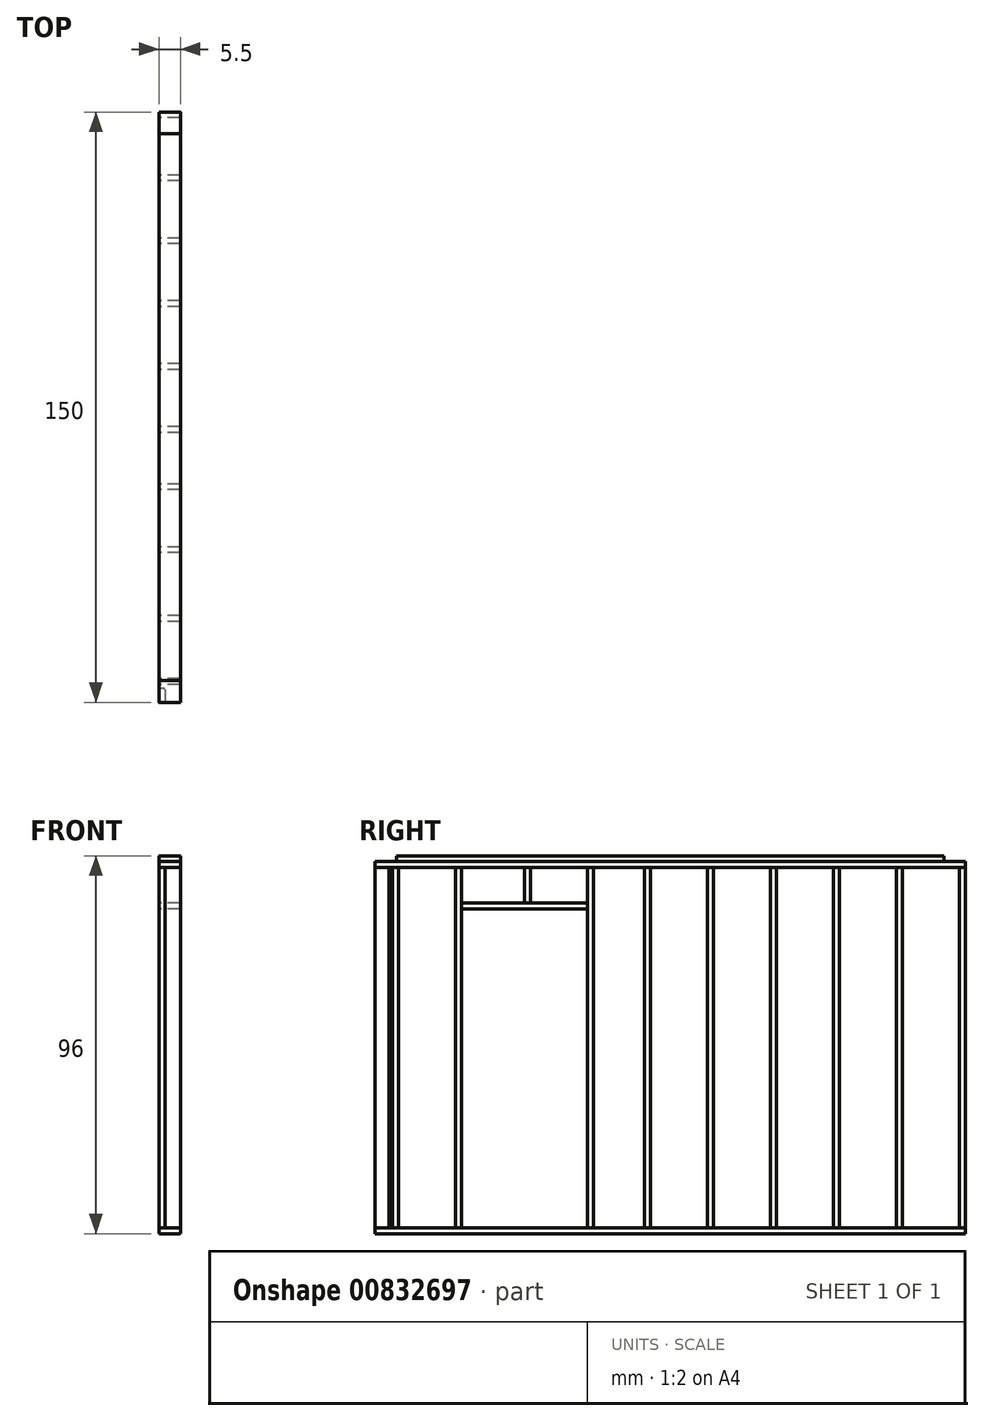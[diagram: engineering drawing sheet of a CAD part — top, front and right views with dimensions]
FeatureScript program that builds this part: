
annotation { "Feature Type Name" : "Feature", "Feature Type Description" : "" }
export const myFeature = defineFeature(function(context is Context, id is Id, definition is map)
    precondition{}
    {
        {
            var Q0;
            Q0=qCreatedBy(makeId("Right.planeOp"),FACE);
            var sketch = newSketch(context, id + "F0", { "sketchPlane" : qUnion([Q0])});
            skLineSegment(sketch, "E0.bottom", {"start": v(-65.32, -18.14) * mm, "end": v(84.68, -18.14) * mm});
            skLineSegment(sketch, "E0.top", {"start": v(-65.32, -16.64) * mm, "end": v(84.68, -16.64) * mm});
            skLineSegment(sketch, "E0.left", {"start": v(-65.32, -18.14) * mm, "end": v(-65.32, -16.64) * mm});
            skLineSegment(sketch, "E0.right", {"start": v(84.68, -18.14) * mm, "end": v(84.68, -16.64) * mm});
            skSolve(sketch);
        }
        {
            var Q0;
            Q0 = qSketchRegion(id + "F0", true);
            extrude(context, id + "F1", {"entities" : qUnion([Q0]), "depth" : 5.5 * mm, "offsetDistance" : 25 * mm});
        }
        {
            var Q0;
            Q0=qCreatedBy(makeId("Right.planeOp"),FACE);
            var sketch = newSketch(context, id + "F2", { "sketchPlane" : qUnion([Q0])});
            skLineSegment(sketch, "E1.bottom", {"start": v(84.68, -16.64) * mm, "end": v(83.18, -16.64) * mm});
            skLineSegment(sketch, "E1.top", {"start": v(84.68, 74.86) * mm, "end": v(83.18, 74.86) * mm});
            skLineSegment(sketch, "E1.left", {"start": v(84.68, -16.64) * mm, "end": v(84.68, 74.86) * mm});
            skLineSegment(sketch, "E1.right", {"start": v(83.18, -16.64) * mm, "end": v(83.18, 74.86) * mm});
            skLineSegment(sketch, "E2.1.0.0", {"start": v(67.18, -16.64) * mm, "end": v(67.18, 74.86) * mm});
            skLineSegment(sketch, "E2.1.0.1", {"start": v(68.68, -16.64) * mm, "end": v(68.68, 74.86) * mm});
            skLineSegment(sketch, "E2.1.0.2", {"start": v(68.68, 74.86) * mm, "end": v(67.18, 74.86) * mm});
            skLineSegment(sketch, "E2.1.0.3", {"start": v(68.68, -16.64) * mm, "end": v(67.18, -16.64) * mm});
            skLineSegment(sketch, "E2.2.0.0", {"start": v(51.18, -16.64) * mm, "end": v(51.18, 74.86) * mm});
            skLineSegment(sketch, "E2.2.0.1", {"start": v(52.68, -16.64) * mm, "end": v(52.68, 74.86) * mm});
            skLineSegment(sketch, "E2.2.0.2", {"start": v(52.68, 74.86) * mm, "end": v(51.18, 74.86) * mm});
            skLineSegment(sketch, "E2.2.0.3", {"start": v(52.68, -16.64) * mm, "end": v(51.18, -16.64) * mm});
            skLineSegment(sketch, "E2.3.0.0", {"start": v(35.18, -16.64) * mm, "end": v(35.18, 74.86) * mm});
            skLineSegment(sketch, "E2.3.0.1", {"start": v(36.68, -16.64) * mm, "end": v(36.68, 74.86) * mm});
            skLineSegment(sketch, "E2.3.0.2", {"start": v(36.68, 74.86) * mm, "end": v(35.18, 74.86) * mm});
            skLineSegment(sketch, "E2.3.0.3", {"start": v(36.68, -16.64) * mm, "end": v(35.18, -16.64) * mm});
            skLineSegment(sketch, "E2.4.0.0", {"start": v(19.18, -16.64) * mm, "end": v(19.18, 74.86) * mm});
            skLineSegment(sketch, "E2.4.0.1", {"start": v(20.68, -16.64) * mm, "end": v(20.68, 74.86) * mm});
            skLineSegment(sketch, "E2.4.0.2", {"start": v(20.68, 74.86) * mm, "end": v(19.18, 74.86) * mm});
            skLineSegment(sketch, "E2.4.0.3", {"start": v(20.68, -16.64) * mm, "end": v(19.18, -16.64) * mm});
            skLineSegment(sketch, "E2.5.0.0", {"start": v(3.18, -16.64) * mm, "end": v(3.18, 74.86) * mm});
            skLineSegment(sketch, "E2.5.0.1", {"start": v(4.68, -16.64) * mm, "end": v(4.68, 74.86) * mm});
            skLineSegment(sketch, "E2.5.0.2", {"start": v(4.68, 74.86) * mm, "end": v(3.18, 74.86) * mm});
            skLineSegment(sketch, "E2.5.0.3", {"start": v(4.68, -16.64) * mm, "end": v(3.18, -16.64) * mm});
            skLineSegment(sketch, "E2.6.0.0", {"start": v(-11.32, -16.64) * mm, "end": v(-11.32, 74.86) * mm});
            skLineSegment(sketch, "E2.6.0.1", {"start": v(-9.82, -16.64) * mm, "end": v(-9.82, 74.86) * mm});
            skLineSegment(sketch, "E2.6.0.2", {"start": v(-9.82, 74.86) * mm, "end": v(-11.32, 74.86) * mm});
            skLineSegment(sketch, "E2.6.0.3", {"start": v(-9.82, -16.64) * mm, "end": v(-11.32, -16.64) * mm});
            skLineSegment(sketch, "E2.8.0.0", {"start": v(-44.82, -16.64) * mm, "end": v(-44.82, 74.86) * mm});
            skLineSegment(sketch, "E2.8.0.1", {"start": v(-43.32, -16.64) * mm, "end": v(-43.32, 74.86) * mm});
            skLineSegment(sketch, "E2.8.0.2", {"start": v(-43.32, 74.86) * mm, "end": v(-44.82, 74.86) * mm});
            skLineSegment(sketch, "E2.8.0.3", {"start": v(-43.32, -16.64) * mm, "end": v(-44.82, -16.64) * mm});
            skLineSegment(sketch, "E2.9.0.0", {"start": v(-60.82, -16.64) * mm, "end": v(-60.82, 74.86) * mm});
            skLineSegment(sketch, "E2.9.0.1", {"start": v(-59.32, -16.64) * mm, "end": v(-59.32, 74.86) * mm});
            skLineSegment(sketch, "E2.9.0.2", {"start": v(-59.32, 74.86) * mm, "end": v(-60.82, 74.86) * mm});
            skLineSegment(sketch, "E2.9.0.3", {"start": v(-59.32, -16.64) * mm, "end": v(-60.82, -16.64) * mm});
            skLineSegment(sketch, "E2.direction1", {"start": v(83.18, -16.64) * mm, "end": v(67.18, -16.64) * mm, "construction": true});
            skPoint(sketch, "E3.endSnap0", {"position": v(-60.07, -16.64) * mm});
            skSolve(sketch);
        }
        {
            var Q0;
            Q0 = qSketchRegion(id + "F2", true);
            extrude(context, id + "F3", {"entities" : qUnion([Q0]), "depth" : 5.5 * mm, "offsetDistance" : 25 * mm});
        }
        {
            var Q0;
            Q0=qCreatedBy(makeId("Right.planeOp"),FACE);
            var sketch = newSketch(context, id + "F4", { "sketchPlane" : qUnion([Q0])});
            skLineSegment(sketch, "E4.bottom", {"start": v(84.68, 74.86) * mm, "end": v(-65.32, 74.86) * mm});
            skLineSegment(sketch, "E4.top", {"start": v(84.68, 76.36) * mm, "end": v(-65.32, 76.36) * mm});
            skLineSegment(sketch, "E4.left", {"start": v(84.68, 74.86) * mm, "end": v(84.68, 76.36) * mm});
            skLineSegment(sketch, "E4.right", {"start": v(-65.32, 74.86) * mm, "end": v(-65.32, 76.36) * mm});
            skLineSegment(sketch, "E5.bottom", {"start": v(79.18, 76.36) * mm, "end": v(-59.82, 76.36) * mm});
            skLineSegment(sketch, "E6.bottom", {"start": v(-11.32, 64.36) * mm, "end": v(-43.32, 64.36) * mm});
            skLineSegment(sketch, "E6.top", {"start": v(-11.32, 65.86) * mm, "end": v(-43.32, 65.86) * mm});
            skLineSegment(sketch, "E6.left", {"start": v(-11.32, 64.36) * mm, "end": v(-11.32, 65.86) * mm});
            skLineSegment(sketch, "E6.right", {"start": v(-43.32, 64.36) * mm, "end": v(-43.32, 65.86) * mm});
            skSolve(sketch);
        }
        {
            var Q0;
            Q0 = qSketchRegion(id + "F4", true);
            extrude(context, id + "F5", {"entities" : qUnion([Q0]), "depth" : 5.5 * mm, "offsetDistance" : 25 * mm});
        }
        {
            var Q0;
            Q0=qCreatedBy(makeId("Right.planeOp"),FACE);
            var sketch = newSketch(context, id + "F6", { "sketchPlane" : qUnion([Q0])});
            skLineSegment(sketch, "E7.bottom", {"start": v(79.18, 76.36) * mm, "end": v(-59.82, 76.36) * mm});
            skLineSegment(sketch, "E7.top", {"start": v(79.18, 77.86) * mm, "end": v(-59.82, 77.86) * mm});
            skLineSegment(sketch, "E7.left", {"start": v(79.18, 76.36) * mm, "end": v(79.18, 77.86) * mm});
            skLineSegment(sketch, "E7.right", {"start": v(-59.82, 76.36) * mm, "end": v(-59.82, 77.86) * mm});
            skLineSegment(sketch, "E8.bottom", {"start": v(-25.82, 74.86) * mm, "end": v(-27.32, 74.86) * mm});
            skLineSegment(sketch, "E8.top", {"start": v(-25.82, 65.86) * mm, "end": v(-27.32, 65.86) * mm});
            skLineSegment(sketch, "E8.left", {"start": v(-25.82, 74.86) * mm, "end": v(-25.82, 65.86) * mm});
            skLineSegment(sketch, "E8.right", {"start": v(-27.32, 74.86) * mm, "end": v(-27.32, 65.86) * mm});
            skSolve(sketch);
        }
        {
            var Q0;
            Q0 = qSketchRegion(id + "F6", true);
            extrude(context, id + "F7", {"entities" : qUnion([Q0]), "depth" : 5.5 * mm, "offsetDistance" : 25 * mm});
        }
        {
            var Q0;
            Q0=makeQuery(id+"F3.opExtrude","CAP_EDGE",EDGE,{"disambiguationData":[OSD([sQuery(id+"F2.wireOp",EDGE,"E2.4.0.1")])],"isStart":true});
            var Q1;
            Q1=makeQuery(id+"F3.opExtrude","CAP_EDGE",EDGE,{"disambiguationData":[OSD([sQuery(id+"F2.wireOp",EDGE,"E2.5.0.0")])],"isStart":true});
            var Q2;
            Q2=makeQuery(id+"F3.opExtrude","CAP_EDGE",EDGE,{"disambiguationData":[OSD([sQuery(id+"F2.wireOp",EDGE,"E2.1.0.0")])],"isStart":true});
            var Q3;
            Q3=makeQuery(id+"F3.opExtrude","CAP_EDGE",EDGE,{"disambiguationData":[OSD([sQuery(id+"F2.wireOp",EDGE,"E2.1.0.1")])],"isStart":true});
            var Q4;
            Q4=makeQuery(id+"F3.opExtrude","CAP_EDGE",EDGE,{"disambiguationData":[OSD([sQuery(id+"F2.wireOp",EDGE,"E2.1.0.1")])],"isStart":false});
            var Q5;
            Q5=makeQuery(id+"F3.opExtrude","CAP_EDGE",EDGE,{"disambiguationData":[OSD([sQuery(id+"F2.wireOp",EDGE,"E2.3.0.0")])],"isStart":true});
            var Q6;
            Q6=makeQuery(id+"F3.opExtrude","CAP_EDGE",EDGE,{"disambiguationData":[OSD([sQuery(id+"F2.wireOp",EDGE,"E2.3.0.1")])],"isStart":false});
            var Q7;
            Q7=makeQuery(id+"F3.opExtrude","CAP_EDGE",EDGE,{"disambiguationData":[OSD([sQuery(id+"F2.wireOp",EDGE,"E2.3.0.1")])],"isStart":true});
            var Q8;
            Q8=makeQuery(id+"F3.opExtrude","CAP_EDGE",EDGE,{"disambiguationData":[OSD([sQuery(id+"F2.wireOp",EDGE,"E2.2.0.0")])],"isStart":true});
            var Q9;
            Q9=makeQuery(id+"F3.opExtrude","CAP_EDGE",EDGE,{"disambiguationData":[OSD([sQuery(id+"F2.wireOp",EDGE,"E2.2.0.1")])],"isStart":false});
            var Q10;
            Q10=makeQuery(id+"F3.opExtrude","CAP_EDGE",EDGE,{"disambiguationData":[OSD([sQuery(id+"F2.wireOp",EDGE,"E2.2.0.1")])],"isStart":true});
            var Q11;
            Q11=makeQuery(id+"F3.opExtrude","CAP_EDGE",EDGE,{"disambiguationData":[OSD([sQuery(id+"F2.wireOp",EDGE,"t0kMXWXi-M4ia-VZsh-PzWo-nqMn7ONUEsGX.right")])],"isStart":true});
            var Q12;
            Q12=makeQuery(id+"F3.opExtrude","CAP_EDGE",EDGE,{"disambiguationData":[OSD([sQuery(id+"F2.wireOp",EDGE,"t0kMXWXi-M4ia-VZsh-PzWo-nqMn7ONUEsGX.left")])],"isStart":false});
            var Q13;
            Q13=makeQuery(id+"F3.opExtrude","CAP_EDGE",EDGE,{"disambiguationData":[OSD([sQuery(id+"F2.wireOp",EDGE,"t0kMXWXi-M4ia-VZsh-PzWo-nqMn7ONUEsGX.left")])],"isStart":true});
            var Q14;
            Q14=makeQuery(id+"F3.opExtrude","CAP_EDGE",EDGE,{"disambiguationData":[OSD([sQuery(id+"F2.wireOp",EDGE,"E1.left")])],"isStart":false});
            var Q15;
            Q15=makeQuery(id+"F3.opExtrude","CAP_EDGE",EDGE,{"disambiguationData":[OSD([sQuery(id+"F2.wireOp",EDGE,"E1.left")])],"isStart":true});
            var Q16;
            Q16=makeQuery(id+"F3.opExtrude","CAP_EDGE",EDGE,{"disambiguationData":[OSD([sQuery(id+"F2.wireOp",EDGE,"E2.8.0.1")])],"isStart":false});
            var Q17;
            Q17=makeQuery(id+"F3.opExtrude","CAP_EDGE",EDGE,{"disambiguationData":[OSD([sQuery(id+"F2.wireOp",EDGE,"E2.8.0.0")])],"isStart":true});
            var Q18;
            Q18=makeQuery(id+"F3.opExtrude","CAP_EDGE",EDGE,{"disambiguationData":[OSD([sQuery(id+"F2.wireOp",EDGE,"E2.8.0.1")])],"isStart":true});
            var Q19;
            Q19=makeQuery(id+"F3.opExtrude","CAP_EDGE",EDGE,{"disambiguationData":[OSD([sQuery(id+"F2.wireOp",EDGE,"E2.8.0.0")])],"isStart":false});
            var Q20;
            Q20=makeQuery(id+"F3.opExtrude","CAP_EDGE",EDGE,{"disambiguationData":[OSD([sQuery(id+"F2.wireOp",EDGE,"E2.4.0.1")])],"isStart":false});
            var Q21;
            Q21=makeQuery(id+"F3.opExtrude","CAP_EDGE",EDGE,{"disambiguationData":[OSD([sQuery(id+"F2.wireOp",EDGE,"E2.4.0.0")])],"isStart":true});
            var Q22;
            Q22=makeQuery(id+"F3.opExtrude","CAP_EDGE",EDGE,{"disambiguationData":[OSD([sQuery(id+"F2.wireOp",EDGE,"E2.4.0.0")])],"isStart":false});
            var Q23;
            Q23=makeQuery(id+"F3.opExtrude","CAP_EDGE",EDGE,{"disambiguationData":[OSD([sQuery(id+"F2.wireOp",EDGE,"E2.5.0.1")])],"isStart":false});
            var Q24;
            Q24=makeQuery(id+"F3.opExtrude","CAP_EDGE",EDGE,{"disambiguationData":[OSD([sQuery(id+"F2.wireOp",EDGE,"E2.5.0.0")])],"isStart":false});
            var Q25;
            Q25=makeQuery(id+"F3.opExtrude","CAP_EDGE",EDGE,{"disambiguationData":[OSD([sQuery(id+"F2.wireOp",EDGE,"E2.5.0.1")])],"isStart":true});
            var Q26;
            Q26=makeQuery(id+"F3.opExtrude","CAP_EDGE",EDGE,{"disambiguationData":[OSD([sQuery(id+"F2.wireOp",EDGE,"E2.9.0.1")])],"isStart":true});
            var Q27;
            Q27=makeQuery(id+"F3.opExtrude","CAP_EDGE",EDGE,{"disambiguationData":[OSD([sQuery(id+"F2.wireOp",EDGE,"E2.9.0.0")])],"isStart":false});
            var Q28;
            Q28=makeQuery(id+"F3.opExtrude","CAP_EDGE",EDGE,{"disambiguationData":[OSD([sQuery(id+"F2.wireOp",EDGE,"E2.9.0.0")])],"isStart":true});
            var Q29;
            Q29=makeQuery(id+"F3.opExtrude","CAP_EDGE",EDGE,{"disambiguationData":[OSD([sQuery(id+"F2.wireOp",EDGE,"E2.9.0.1")])],"isStart":false});
            var Q30;
            Q30=makeQuery(id+"F3.opExtrude","CAP_EDGE",EDGE,{"disambiguationData":[OSD([sQuery(id+"F2.wireOp",EDGE,"E2.6.0.0")])],"isStart":false});
            var Q31;
            Q31=makeQuery(id+"F3.opExtrude","CAP_EDGE",EDGE,{"disambiguationData":[OSD([sQuery(id+"F2.wireOp",EDGE,"E2.6.0.1")])],"isStart":true});
            var Q32;
            Q32=makeQuery(id+"F3.opExtrude","CAP_EDGE",EDGE,{"disambiguationData":[OSD([sQuery(id+"F2.wireOp",EDGE,"E2.6.0.1")])],"isStart":false});
            var Q33;
            Q33=makeQuery(id+"F3.opExtrude","CAP_EDGE",EDGE,{"disambiguationData":[OSD([sQuery(id+"F2.wireOp",EDGE,"E2.6.0.0")])],"isStart":true});
            var Q34;
            Q34=makeQuery(id+"F3.opExtrude","CAP_EDGE",EDGE,{"disambiguationData":[OSD([sQuery(id+"F2.wireOp",EDGE,"E2.1.0.0")])],"isStart":false});
            var Q35;
            Q35=makeQuery(id+"F3.opExtrude","CAP_EDGE",EDGE,{"disambiguationData":[OSD([sQuery(id+"F2.wireOp",EDGE,"E2.3.0.0")])],"isStart":false});
            var Q36;
            Q36=makeQuery(id+"F3.opExtrude","CAP_EDGE",EDGE,{"disambiguationData":[OSD([sQuery(id+"F2.wireOp",EDGE,"E2.2.0.0")])],"isStart":false});
            var Q37;
            Q37=makeQuery(id+"F3.opExtrude","CAP_EDGE",EDGE,{"disambiguationData":[OSD([sQuery(id+"F2.wireOp",EDGE,"t0kMXWXi-M4ia-VZsh-PzWo-nqMn7ONUEsGX.right")])],"isStart":false});
            var Q38;
            Q38=makeQuery(id+"F3.opExtrude","CAP_EDGE",EDGE,{"disambiguationData":[OSD([sQuery(id+"F2.wireOp",EDGE,"E1.right")])],"isStart":true});
            var Q39;
            Q39=makeQuery(id+"F3.opExtrude","CAP_EDGE",EDGE,{"disambiguationData":[OSD([sQuery(id+"F2.wireOp",EDGE,"E1.right")])],"isStart":false});
            var Q40;
            Q40=makeQuery(id+"F5.opExtrude","CAP_EDGE",EDGE,{"disambiguationData":[OSD([sQuery(id+"F4.wireOp",EDGE,"E6.top")])],"isStart":false});
            var Q41;
            Q41=makeQuery(id+"F5.opExtrude","CAP_EDGE",EDGE,{"disambiguationData":[OSD([sQuery(id+"F4.wireOp",EDGE,"E6.bottom")])],"isStart":true});
            var Q42;
            Q42=makeQuery(id+"F5.opExtrude","CAP_EDGE",EDGE,{"disambiguationData":[OSD([sQuery(id+"F4.wireOp",EDGE,"E6.bottom")])],"isStart":false});
            var Q43;
            Q43=makeQuery(id+"F5.opExtrude","CAP_EDGE",EDGE,{"disambiguationData":[OSD([sQuery(id+"F4.wireOp",EDGE,"E6.top")])],"isStart":true});
            var Q44;
            Q44=makeQuery(id+"F7.opExtrude","CAP_EDGE",EDGE,{"disambiguationData":[OSD([sQuery(id+"F6.wireOp",EDGE,"E7.top")])],"isStart":true});
            var Q45;
            Q45=makeQuery(id+"F7.opExtrude","CAP_EDGE",EDGE,{"disambiguationData":[OSD([sQuery(id+"F6.wireOp",EDGE,"E7.top")])],"isStart":false});
            var Q46;
            Q46=makeQuery(id+"F5.opExtrude","CAP_EDGE",EDGE,{"disambiguationData":[OSD([sQuery(id+"F4.wireOp",EDGE,"E4.bottom")])],"isStart":false});
            var Q47;
            Q47=makeQuery(id+"F5.opExtrude","CAP_EDGE",EDGE,{"disambiguationData":[OSD([sQuery(id+"F4.wireOp",EDGE,"E4.top"),sQuery(id+"F4.wireOp",EDGE,"E5.bottom")])],"isStart":true});
            var Q48;
            Q48=makeQuery(id+"F5.opExtrude","CAP_EDGE",EDGE,{"disambiguationData":[OSD([sQuery(id+"F4.wireOp",EDGE,"E4.top"),sQuery(id+"F4.wireOp",EDGE,"E5.bottom")])],"isStart":false});
            var Q49;
            Q49=makeQuery(id+"F5.opExtrude","CAP_EDGE",EDGE,{"disambiguationData":[OSD([sQuery(id+"F4.wireOp",EDGE,"E4.bottom")])],"isStart":true});
            var Q50;
            Q50=makeQuery(id+"F7.opExtrude","CAP_EDGE",EDGE,{"disambiguationData":[OSD([sQuery(id+"F6.wireOp",EDGE,"E7.bottom")])],"isStart":true});
            var Q51;
            Q51=makeQuery(id+"F7.opExtrude","CAP_EDGE",EDGE,{"disambiguationData":[OSD([sQuery(id+"F6.wireOp",EDGE,"E7.bottom")])],"isStart":false});
            var Q52;
            Q52=makeQuery(id+"F1.opExtrude","CAP_EDGE",EDGE,{"disambiguationData":[OSD([sQuery(id+"F0.wireOp",EDGE,"E0.bottom")])],"isStart":true});
            var Q53;
            Q53=makeQuery(id+"F1.opExtrude","CAP_EDGE",EDGE,{"disambiguationData":[OSD([sQuery(id+"F0.wireOp",EDGE,"E0.top")])],"isStart":true});
            var Q54;
            Q54=makeQuery(id+"F1.opExtrude","CAP_EDGE",EDGE,{"disambiguationData":[OSD([sQuery(id+"F0.wireOp",EDGE,"E0.top")])],"isStart":false});
            var Q55;
            Q55=makeQuery(id+"F1.opExtrude","CAP_EDGE",EDGE,{"disambiguationData":[OSD([sQuery(id+"F0.wireOp",EDGE,"E0.bottom")])],"isStart":false});
            var Q56;
            Q56=makeQuery(id+"F7.opExtrude","CAP_EDGE",EDGE,{"disambiguationData":[OSD([sQuery(id+"F6.wireOp",EDGE,"E8.left")])],"isStart":false});
            var Q57;
            Q57=makeQuery(id+"F7.opExtrude","CAP_EDGE",EDGE,{"disambiguationData":[OSD([sQuery(id+"F6.wireOp",EDGE,"E8.right")])],"isStart":false});
            var Q58;
            Q58=makeQuery(id+"F7.opExtrude","CAP_EDGE",EDGE,{"disambiguationData":[OSD([sQuery(id+"F6.wireOp",EDGE,"E8.right")])],"isStart":true});
            var Q59;
            Q59=makeQuery(id+"F7.opExtrude","CAP_EDGE",EDGE,{"disambiguationData":[OSD([sQuery(id+"F6.wireOp",EDGE,"E8.left")])],"isStart":true});
            fillet(context, id + "F8", {"entities" : qUnion([Q0, Q1, Q2, Q3, Q4, Q5, Q6, Q7, Q8, Q9, Q10, Q11, Q12, Q13, Q14, Q15, Q16, Q17, Q18, Q19, Q20, Q21, Q22, Q23, Q24, Q25, Q26, Q27, Q28, Q29, Q30, Q31, Q32, Q33, Q34, Q35, Q36, Q37, Q38, Q39, Q40, Q41, Q42, Q43, Q44, Q45, Q46, Q47, Q48, Q49, Q50, Q51, Q52, Q53, Q54, Q55, Q56, Q57, Q58, Q59]), "radius" : 0.25 * mm, "tangentPropagation" : true, "allowEdgeOverflow" : false});
        }
        {
            var Q0;
            Q0=qCreatedBy(makeId("Right.planeOp"),FACE);
            var sketch = newSketch(context, id + "F9", { "sketchPlane" : qUnion([Q0])});
            skLineSegment(sketch, "E9.bottom", {"start": v(-61.82, -16.64) * mm, "end": v(-65.32, -16.64) * mm});
            skLineSegment(sketch, "E9.top", {"start": v(-61.82, 74.86) * mm, "end": v(-65.32, 74.86) * mm});
            skLineSegment(sketch, "E9.left", {"start": v(-61.82, -16.64) * mm, "end": v(-61.82, 74.86) * mm});
            skLineSegment(sketch, "E9.right", {"start": v(-65.32, -16.64) * mm, "end": v(-65.32, 74.86) * mm});
            skSolve(sketch);
        }
        {
            var Q0;
            Q0 = qSketchRegion(id + "F9", true);
            extrude(context, id + "F10", {"entities" : qUnion([Q0]), "depth" : 1.5 * mm, "offsetDistance" : 25 * mm});
        }
        {
            var Q0;
            Q0=makeQuery(id+"F10.opExtrude","CAP_EDGE",EDGE,{"disambiguationData":[OSD([sQuery(id+"F9.wireOp",EDGE,"E9.left")])],"isStart":true});
            var Q1;
            Q1=makeQuery(id+"F10.opExtrude","CAP_EDGE",EDGE,{"disambiguationData":[OSD([sQuery(id+"F9.wireOp",EDGE,"E9.right")])],"isStart":true});
            var Q2;
            Q2=makeQuery(id+"F10.opExtrude","CAP_EDGE",EDGE,{"disambiguationData":[OSD([sQuery(id+"F9.wireOp",EDGE,"E9.left")])],"isStart":false});
            var Q3;
            Q3=makeQuery(id+"F10.opExtrude","CAP_EDGE",EDGE,{"disambiguationData":[OSD([sQuery(id+"F9.wireOp",EDGE,"E9.right")])],"isStart":false});
            fillet(context, id + "F11", {"entities" : qUnion([Q0, Q1, Q2, Q3]), "radius" : 0.25 * mm, "tangentPropagation" : true, "allowEdgeOverflow" : false});
        }
    });
